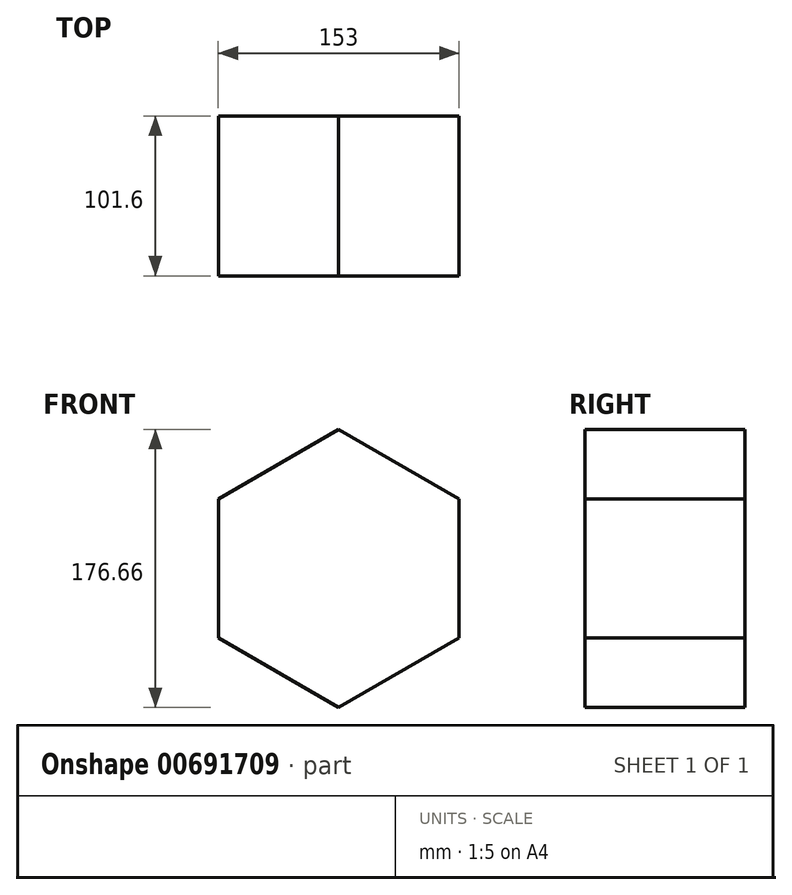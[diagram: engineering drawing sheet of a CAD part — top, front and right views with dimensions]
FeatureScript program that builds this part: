
annotation { "Feature Type Name" : "Feature", "Feature Type Description" : "" }
export const myFeature = defineFeature(function(context is Context, id is Id, definition is map)
    precondition{}
    {
        {
            var Q0;
            Q0=qCreatedBy(makeId("Front.planeOp"),FACE);
            var sketch = newSketch(context, id + "F0", { "sketchPlane" : qUnion([Q0])});
            skCircle(sketch, "E0.cCircle", {"center": v(0, 0) * mm, "radius": 76.5 * mm, "construction": true});
            skLineSegment(sketch, "E0.0", {"start": v(76.5, 44.17) * mm, "end": v(76.5, -44.17) * mm});
            skLineSegment(sketch, "E0.1", {"start": v(76.5, -44.17) * mm, "end": v(0, -88.33) * mm});
            skLineSegment(sketch, "E0.2", {"start": v(0, -88.33) * mm, "end": v(-76.5, -44.17) * mm});
            skLineSegment(sketch, "E0.3", {"start": v(-76.5, -44.17) * mm, "end": v(-76.5, 44.17) * mm});
            skLineSegment(sketch, "E0.4", {"start": v(-76.5, 44.17) * mm, "end": v(0, 88.33) * mm});
            skLineSegment(sketch, "E0.5", {"start": v(0, 88.33) * mm, "end": v(76.5, 44.17) * mm});
            skPoint(sketch, "E0.0.midPoint", {"position": v(76.5, 0) * mm});
            skSolve(sketch);
        }
        {
            var Q0;
            Q0 = qSketchRegion(id + "F0", true);
            extrude(context, id + "F1", {"entities" : qUnion([Q0]), "depth" : 101.6 * mm, "offsetDistance" : 25.4 * mm});
        }
    });
